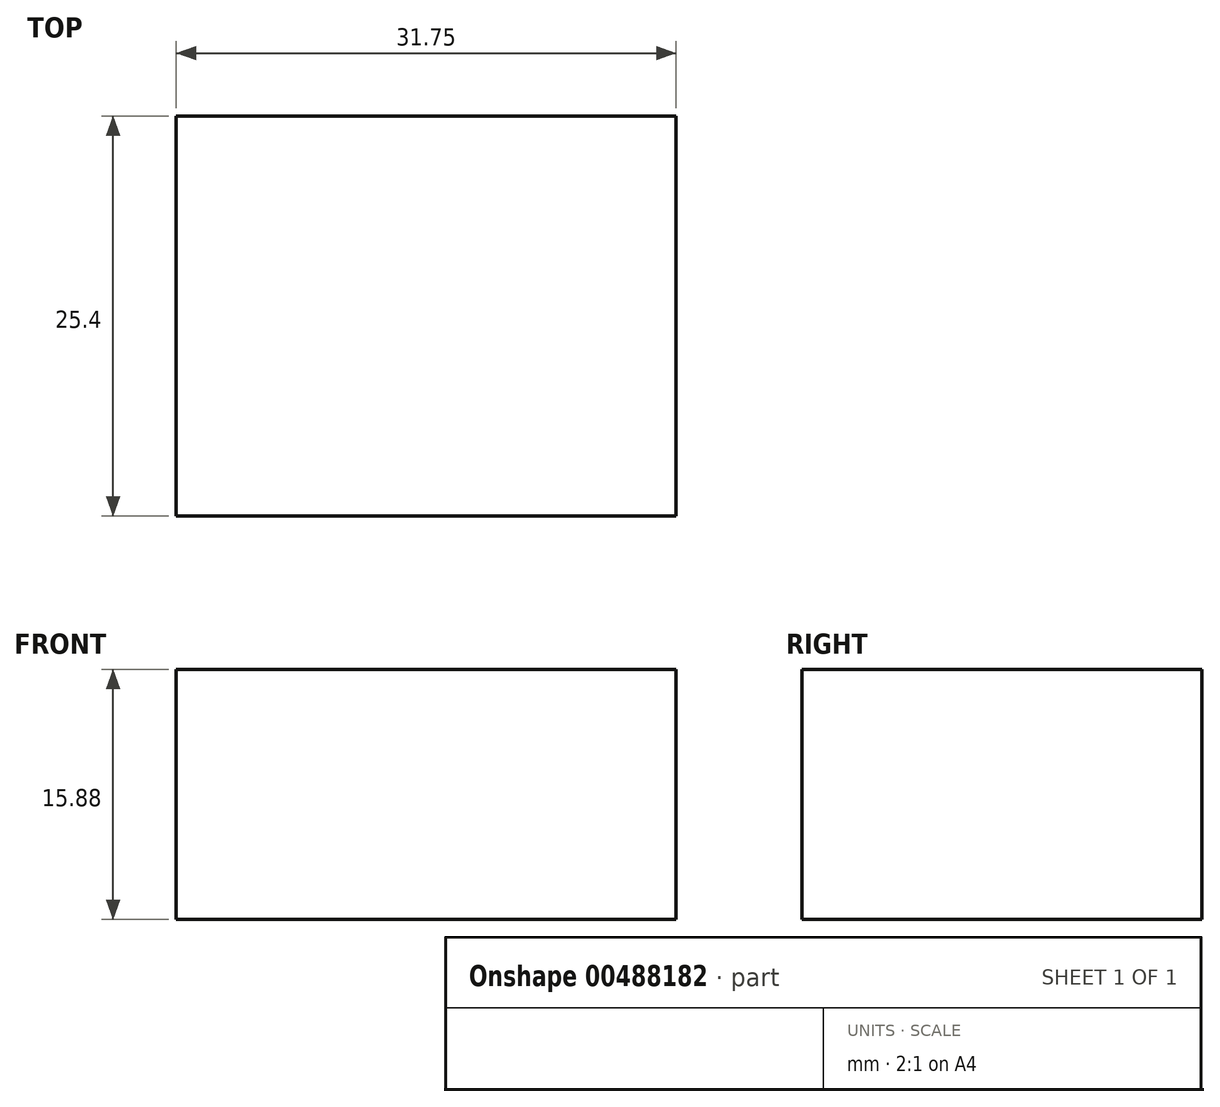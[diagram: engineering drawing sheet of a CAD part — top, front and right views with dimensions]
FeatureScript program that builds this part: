
annotation { "Feature Type Name" : "Feature", "Feature Type Description" : "" }
export const myFeature = defineFeature(function(context is Context, id is Id, definition is map)
    precondition{}
    {
        {
            var Q0;
            Q0=qCreatedBy(makeId("Front.planeOp"),FACE);
            var sketch = newSketch(context, id + "F0", { "sketchPlane" : qUnion([Q0])});
            skLineSegment(sketch, "E0", {"start": v(0, 0) * mm, "end": v(0, 15.88) * mm});
            skLineSegment(sketch, "E1", {"start": v(0, 15.88) * mm, "end": v(31.75, 15.88) * mm});
            skLineSegment(sketch, "E2", {"start": v(31.75, 15.88) * mm, "end": v(31.75, 0) * mm});
            skLineSegment(sketch, "E3", {"start": v(31.75, 0) * mm, "end": v(0, 0) * mm});
            skSolve(sketch);
        }
        {
            var Q0;
            Q0=makeQuery(id+"F0.imprint","IMPRINT",FACE,{"disambiguationData":[TD([[makeQuery(id+"F0.imprint","IMPRINT",EDGE,{"derivedFrom":sQuery(id+"F0.wireOp",EDGE,"E0")}),-1.0]])]});
            extrude(context, id + "F1", {"entities" : qUnion([Q0]), "depth" : 25.4 * mm});
        }
    });
